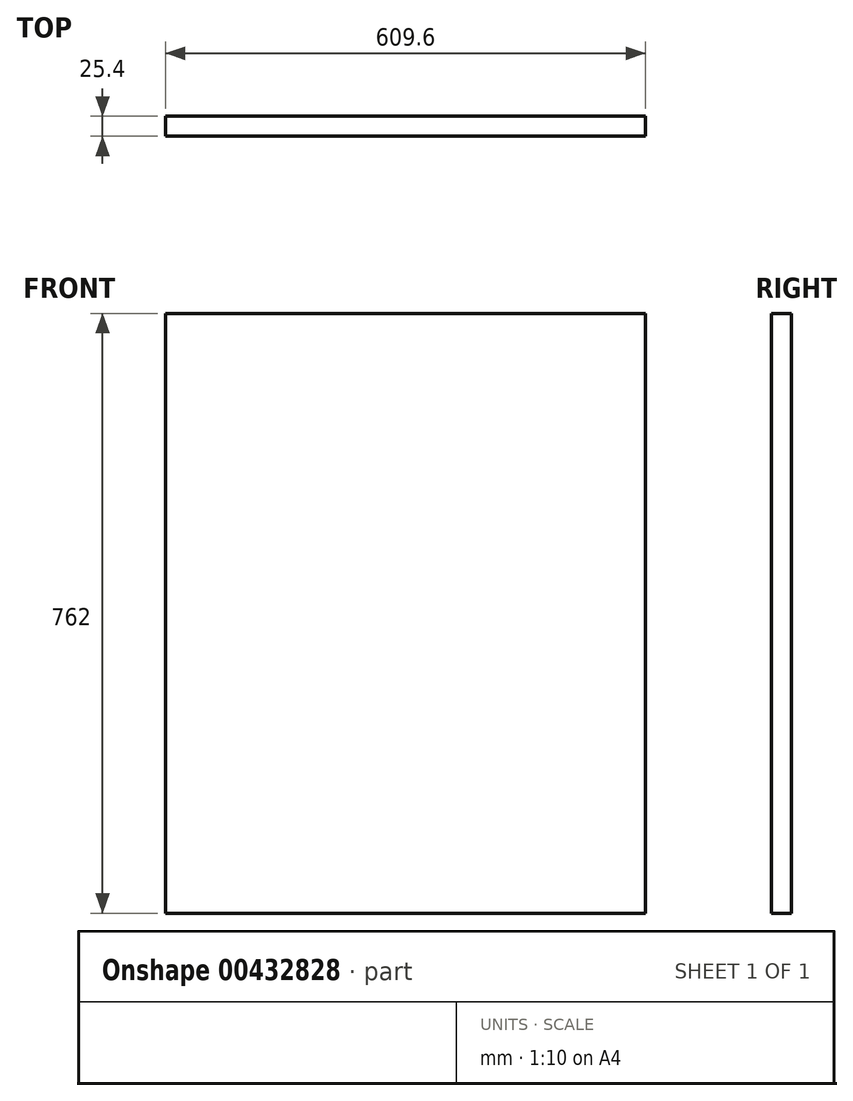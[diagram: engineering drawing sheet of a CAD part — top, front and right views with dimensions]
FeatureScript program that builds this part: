
annotation { "Feature Type Name" : "Feature", "Feature Type Description" : "" }
export const myFeature = defineFeature(function(context is Context, id is Id, definition is map)
    precondition{}
    {
        {
            var Q0;
            Q0=qCreatedBy(makeId("Front.planeOp"),FACE);
            var sketch = newSketch(context, id + "F0", { "sketchPlane" : qUnion([Q0])});
            skLineSegment(sketch, "E0.bottom", {"start": v(68.81, -196.96) * mm, "end": v(-540.79, -196.96) * mm});
            skLineSegment(sketch, "E0.top", {"start": v(68.81, 565.04) * mm, "end": v(-540.79, 565.04) * mm});
            skLineSegment(sketch, "E0.left", {"start": v(68.81, -196.96) * mm, "end": v(68.81, 565.04) * mm});
            skLineSegment(sketch, "E0.right", {"start": v(-540.79, -196.96) * mm, "end": v(-540.79, 565.04) * mm});
            skPoint(sketch, "E0.middle", {"position": v(-235.99, 184.04) * mm});
            skSolve(sketch);
        }
        {
            var Q0;
            Q0 = qSketchRegion(id + "F0", true);
            extrude(context, id + "F1", {"entities" : qUnion([Q0]), "depth" : 25.4 * mm});
        }
    });
